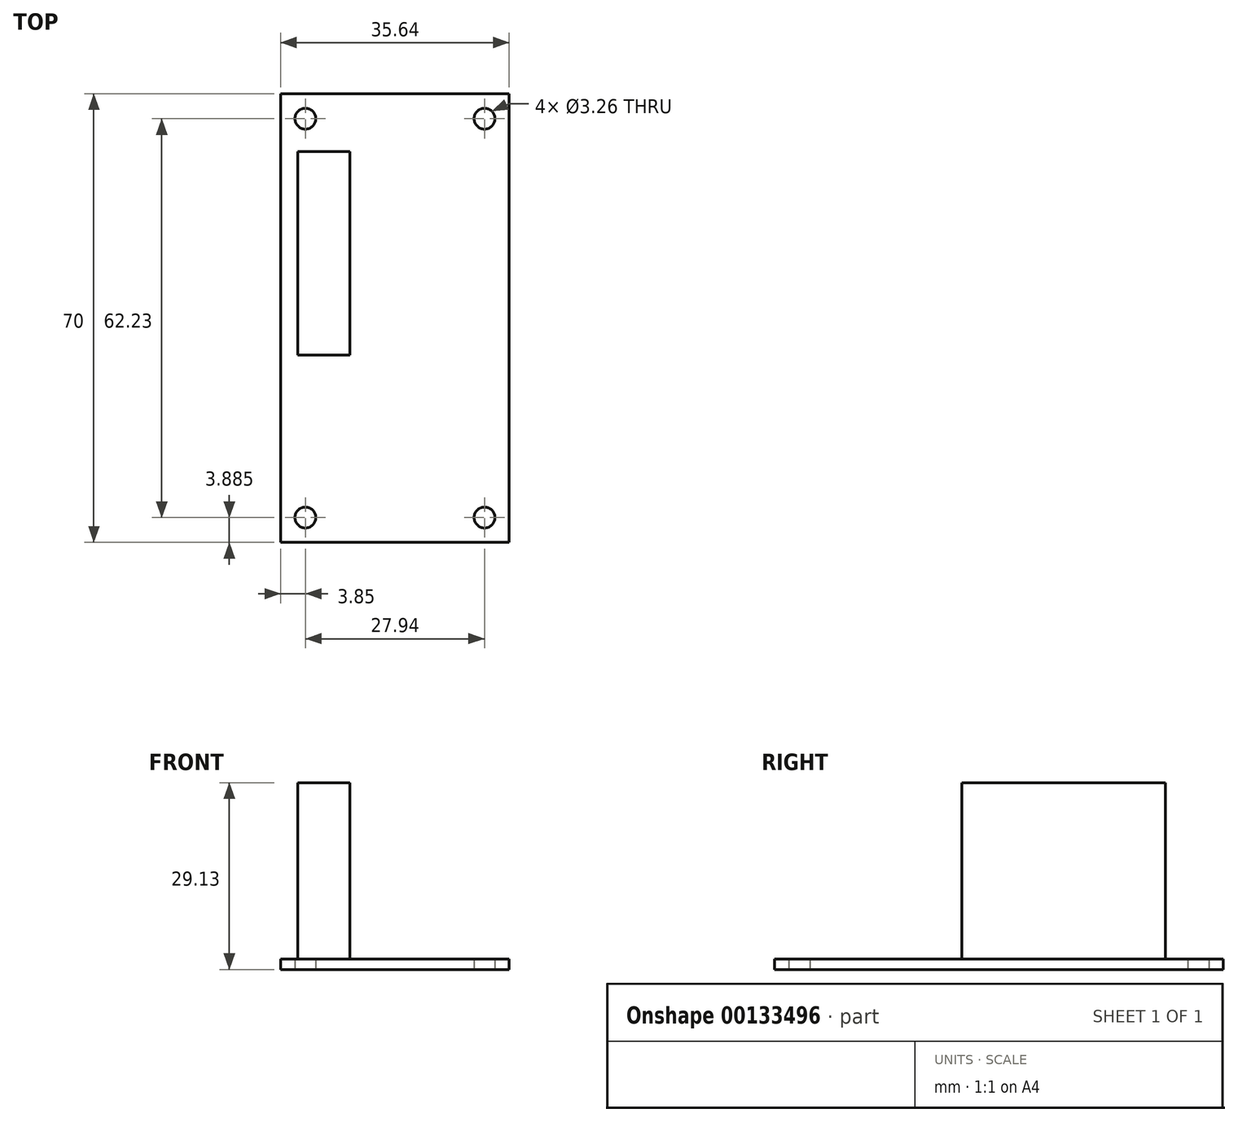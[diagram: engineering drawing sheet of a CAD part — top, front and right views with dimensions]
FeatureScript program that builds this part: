
annotation { "Feature Type Name" : "Feature", "Feature Type Description" : "" }
export const myFeature = defineFeature(function(context is Context, id is Id, definition is map)
    precondition{}
    {
        {
            var Q0;
            Q0=qCreatedBy(makeId("Top.planeOp"),FACE);
            var sketch = newSketch(context, id + "F0", { "sketchPlane" : qUnion([Q0])});
            skLineSegment(sketch, "E0.bottom", {"start": v(17.82, -35) * mm, "end": v(-17.82, -35) * mm});
            skLineSegment(sketch, "E0.top", {"start": v(17.83, 35) * mm, "end": v(-17.82, 35) * mm});
            skLineSegment(sketch, "E0.left", {"start": v(17.82, -35) * mm, "end": v(17.83, 35) * mm});
            skLineSegment(sketch, "E0.right", {"start": v(-17.83, -35) * mm, "end": v(-17.82, 35) * mm});
            skPoint(sketch, "E0.middle", {"position": v(0, 0) * mm});
            skCircle(sketch, "E1", {"center": v(-13.97, 31.12) * mm, "radius": 1.63 * mm});
            skCircle(sketch, "E2", {"center": v(13.97, 31.12) * mm, "radius": 1.63 * mm});
            skCircle(sketch, "E3", {"center": v(13.97, -31.12) * mm, "radius": 1.63 * mm});
            skCircle(sketch, "E4", {"center": v(-13.97, -31.12) * mm, "radius": 1.63 * mm});
            skLineSegment(sketch, "E5.bottom", {"start": v(13.97, -31.12) * mm, "end": v(-13.97, -31.12) * mm, "construction": true});
            skLineSegment(sketch, "E5.top", {"start": v(13.97, 31.12) * mm, "end": v(-13.97, 31.12) * mm, "construction": true});
            skLineSegment(sketch, "E5.left", {"start": v(13.97, -31.12) * mm, "end": v(13.97, 31.12) * mm, "construction": true});
            skLineSegment(sketch, "E5.right", {"start": v(-13.97, -31.12) * mm, "end": v(-13.97, 31.12) * mm, "construction": true});
            skSolve(sketch);
        }
        {
            var Q0;
            Q0 = qSketchRegion(id + "F0", true);
            extrude(context, id + "F1", {"entities" : qUnion([Q0]), "depth" : 1.6 * mm});
        }
        {
            var Q0;
            Q0=makeQuery(id+"F1.opExtrude","CAP_FACE",FACE,{"disambiguationData":[OSD([sQuery(id+"F0.wireOp",EDGE,"E0.bottom"),sQuery(id+"F0.wireOp",EDGE,"E0.top"),sQuery(id+"F0.wireOp",EDGE,"E0.left"),sQuery(id+"F0.wireOp",EDGE,"E0.right"),sQuery(id+"F0.wireOp",EDGE,"E1"),sQuery(id+"F0.wireOp",EDGE,"E2"),sQuery(id+"F0.wireOp",EDGE,"E3"),sQuery(id+"F0.wireOp",EDGE,"E4")])],"isStart":false});
            var sketch = newSketch(context, id + "F2", { "sketchPlane" : qUnion([Q0])});
            skLineSegment(sketch, "E6.bottom", {"start": v(-7, 26) * mm, "end": v(-15.16, 26) * mm});
            skLineSegment(sketch, "E6.top", {"start": v(-7, -5.74) * mm, "end": v(-15.16, -5.74) * mm});
            skLineSegment(sketch, "E6.left", {"start": v(-7, 26) * mm, "end": v(-7, -5.74) * mm});
            skLineSegment(sketch, "E6.right", {"start": v(-15.16, 26) * mm, "end": v(-15.16, -5.74) * mm});
            skSolve(sketch);
        }
        {
            var Q0;
            Q0 = qSketchRegion(id + "F2", true);
            extrude(context, id + "F3", {"entities" : qUnion([Q0]), "operationType" : NewBodyOperationType.ADD, "depth" : 27.53 * mm});
        }
    });
